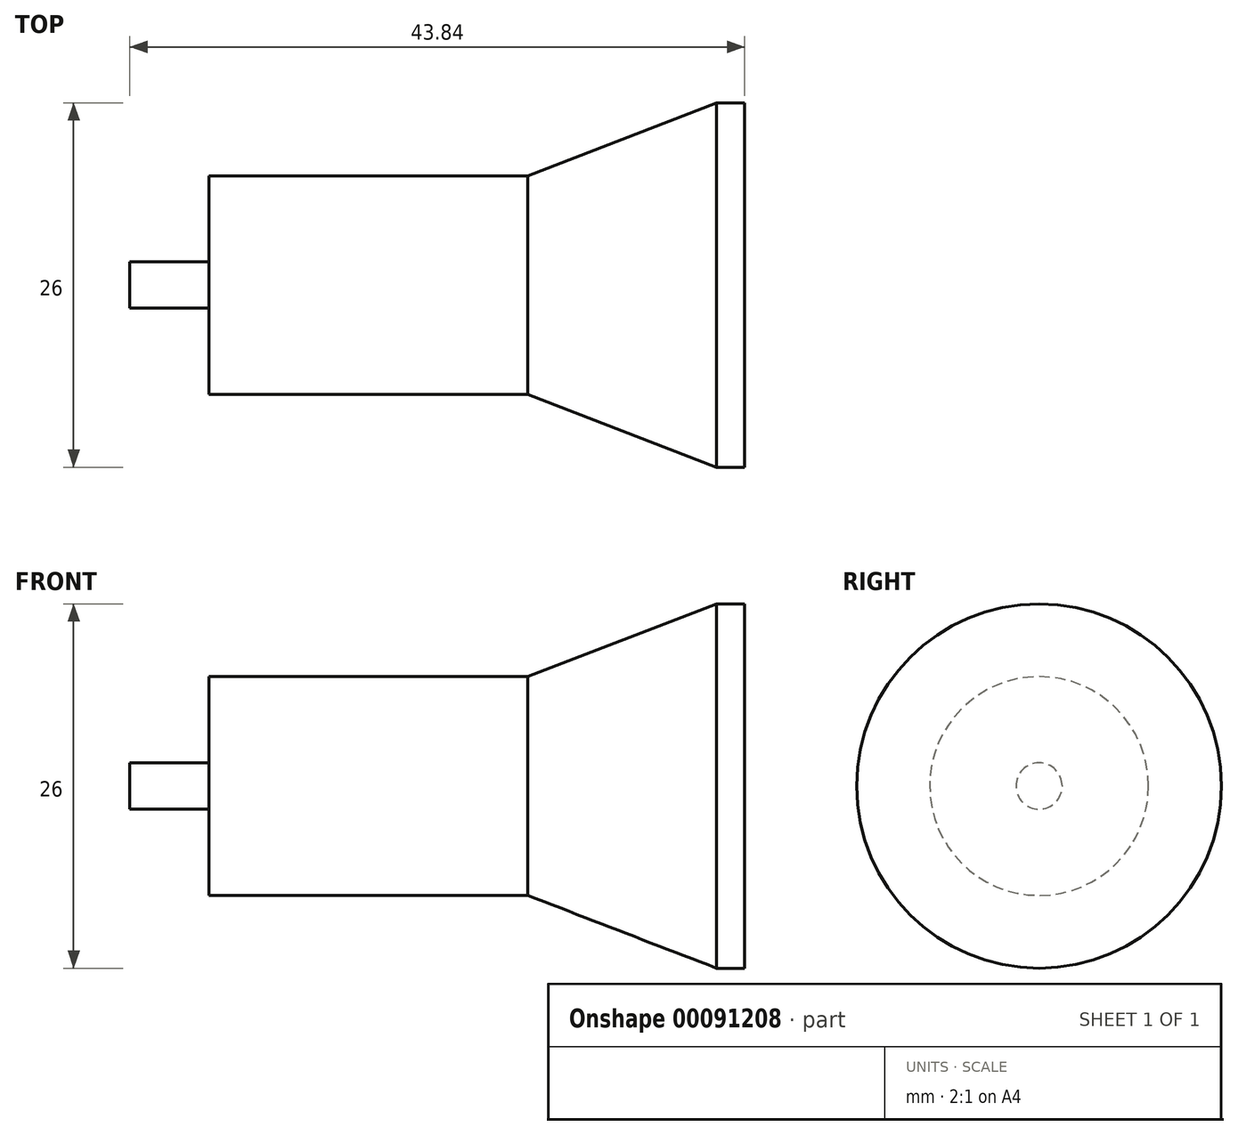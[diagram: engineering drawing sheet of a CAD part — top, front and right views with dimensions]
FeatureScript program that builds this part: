
annotation { "Feature Type Name" : "Feature", "Feature Type Description" : "" }
export const myFeature = defineFeature(function(context is Context, id is Id, definition is map)
    precondition{}
    {
        {
            var Q0;
            Q0=qCreatedBy(makeId("Front.planeOp"),FACE);
            var sketch = newSketch(context, id + "F0", { "sketchPlane" : qUnion([Q0])});
            skLineSegment(sketch, "E0", {"start": v(-53.67, 0) * mm, "end": v(-53.67, 1.65) * mm});
            skLineSegment(sketch, "E1", {"start": v(-48.04, 7.8) * mm, "end": v(-25.3, 7.8) * mm});
            skLineSegment(sketch, "E2", {"start": v(-25.3, 7.8) * mm, "end": v(-11.83, 13) * mm});
            skLineSegment(sketch, "E3", {"start": v(-11.83, 0) * mm, "end": v(-53.67, 0) * mm});
            skLineSegment(sketch, "E4", {"start": v(-25.3, 7.8) * mm, "end": v(-25.3, 0) * mm});
            skLineSegment(sketch, "E5", {"start": v(-48.04, 7.8) * mm, "end": v(-48.04, 1.65) * mm});
            skLineSegment(sketch, "E6", {"start": v(-53.67, 1.65) * mm, "end": v(-48.04, 1.65) * mm});
            skPoint(sketch, "E7.orphan", {"position": v(-48.04, 0) * mm});
            skLineSegment(sketch, "E8", {"start": v(-11.83, 13) * mm, "end": v(-9.83, 13) * mm});
            skLineSegment(sketch, "E9", {"start": v(-9.83, 13) * mm, "end": v(-9.83, 0) * mm});
            skLineSegment(sketch, "E10", {"start": v(-9.83, 0) * mm, "end": v(-11.83, 0) * mm});
            skSolve(sketch);
        }
        {
            var Q0;
            Q0 = qSketchRegion(id + "F0", true);
            var Q1;
            Q1=sQuery(id+"F0.wireOp",EDGE,"E3");
            revolve(context, id + "F1", {"entities" : qUnion([Q0]), "axis" : qUnion([Q1]), "revolveType" : RevolveType.FULL});
        }
    });
